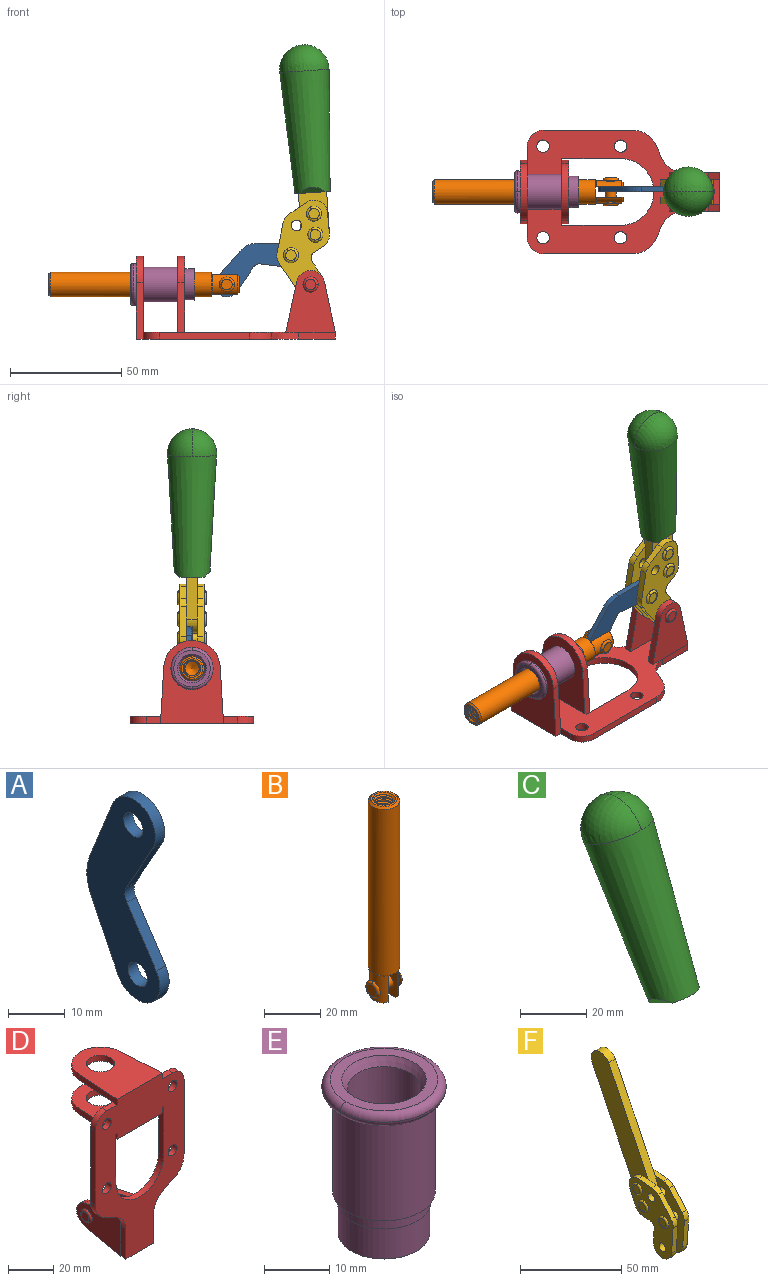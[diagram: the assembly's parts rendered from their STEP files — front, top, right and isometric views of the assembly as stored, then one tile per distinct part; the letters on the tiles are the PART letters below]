
ASSEMBLY  parts=6 mates=6
PART A: 12 faces, bbox 2.3x18.2x42.8 mm
  f0: cylinder r=2.4mm len=4.8mm, axis (1,0,0), area 34.9mm2, adj f4,f11
  f1: cylinder r=10.41mm len=8.47mm, axis (1,0,0), area 20.2mm2, adj f4,f9,f10,f11
  f2: cylinder r=3.05mm len=3.16mm, axis (1,0,0), area 7.7mm2, adj f4,f6,f7,f11
  f3: cylinder r=2.4mm len=4.8mm, axis (1,0,0), area 34.9mm2, adj f4,f11
  f4: plane 42.81x18.23mm, normal (-1,0,0), area 414.1mm2, adj f0,f1,f2,f3,f5,f6,f7,f8
  f5: cylinder r=5.54mm len=10.67mm, axis (1,0,0), area 41.8mm2, adj f4,f6,f10,f11
  f6: plane 11.66x6.53mm, normal (0,-0.87,-0.49), area 30.9mm2, adj f2,f4,f5,f11
  f7: plane 11.17x7.33mm, normal (0,-0.84,0.55), area 30.9mm2, adj f2,f4,f8,f11
  f8: cylinder r=5.54mm len=10.51mm, axis (1,0,0), area 41.8mm2, adj f4,f7,f9,f11
  f9: plane 13.67x6.67mm, normal (0,0.9,-0.44), area 35.1mm2, adj f1,f4,f8,f11
  f10: plane 14.1x5.7mm, normal (0,0.93,0.37), area 35.1mm2, adj f1,f4,f5,f11
  f11: plane 42.81x18.23mm, normal (1,0,0), area 414.1mm2, adj f0,f1,f2,f3,f5,f6,f7,f8
PART B: 48 faces, bbox 12.6x11.1x86.1 mm
  f0: torus R=2.41mm, axis (-1,0,0), area 15mm2, adj f30,f32,f34
  f1: torus R=2.41mm, axis (-1,0,0), area 15mm2, adj f29,f31,f33
  f2: cylinder r=5.54mm len=72.39mm, axis (0,0,1), area 2518.5mm2, adj f3,f4,f42,f43
  f3: cone r=5.54mm half-angle=45deg, axis (0,0,1), area 7.6mm2, adj f2,f5,f41
  f4: cone r=5.54mm half-angle=45deg, axis (0,0,-1), area 34.9mm2, adj f2,f39
  f5: cylinder r=5.08mm len=11.48mm, axis (0,0,1), area 108.3mm2, adj f3,f7,f8,f41
  f6: cylinder r=2.41mm len=4.83mm, axis (-1,0,0), area 71.2mm2, adj f40,f41
  f7: cylinder r=2.41mm len=4.83mm, axis (-1,0,0), area 7.6mm2, adj f5,f34
  f8: cone r=5.08mm half-angle=45deg, axis (0,0,1), area 10.6mm2, adj f5,f37,f41
  f9: cone r=3.98mm half-angle=45deg, axis (0,0,1), area 17.6mm2, adj f27,f39,f45,f46,f47
  f10: cylinder r=2.41mm len=4.83mm, axis (-1,0,0), area 7.6mm2, adj f33,f38
  f11: cylinder r=3.2mm len=6.4mm, axis (0,0,1), area 78.4mm2, adj f12,f28,f44,f45,f47
  f12: cylinder r=3.2mm len=6.4mm, axis (0,0,1), area 10.5mm2, adj f11,f13,f45,f47
  f13: cylinder r=3.2mm len=6.4mm, axis (0,0,1), area 10.5mm2, adj f12,f14,f45,f47
  f14: cylinder r=3.2mm len=6.4mm, axis (0,0,1), area 10.5mm2, adj f13,f15,f45,f47
  f15: cylinder r=3.2mm len=6.4mm, axis (0,0,1), area 10.5mm2, adj f14,f16,f45,f47
  f16: cylinder r=3.2mm len=6.4mm, axis (0,0,1), area 10.5mm2, adj f15,f17,f45,f47
  f17: cylinder r=3.2mm len=6.4mm, axis (0,0,1), area 10.5mm2, adj f16,f18,f45,f47
  f18: cylinder r=3.2mm len=6.4mm, axis (0,0,1), area 10.5mm2, adj f17,f19,f45,f47
  f19: cylinder r=3.2mm len=6.4mm, axis (0,0,1), area 10.5mm2, adj f18,f20,f45,f47
  f20: cylinder r=3.2mm len=6.4mm, axis (0,0,1), area 10.5mm2, adj f19,f21,f45,f47
  f21: cylinder r=3.2mm len=6.4mm, axis (0,0,1), area 10.5mm2, adj f20,f22,f45,f47
  f22: cylinder r=3.2mm len=6.4mm, axis (0,0,1), area 10.5mm2, adj f21,f23,f45,f47
  f23: cylinder r=3.2mm len=6.4mm, axis (0,0,1), area 10.5mm2, adj f22,f24,f45,f47
  f24: cylinder r=3.2mm len=6.4mm, axis (0,0,1), area 10.5mm2, adj f23,f25,f45,f47
  f25: cylinder r=3.2mm len=6.4mm, axis (0,0,1), area 10.5mm2, adj f24,f26,f45,f47
  f26: cylinder r=3.2mm len=6.4mm, axis (0,0,1), area 10.5mm2, adj f25,f27,f45,f47
  f27: cylinder r=3.2mm len=6.4mm, axis (0,0,1), area 7.4mm2, adj f9,f26,f45,f47
  f28: cone r=3.2mm half-angle=60deg, axis (0,0,1), area 37.2mm2, adj f11
  f29: plane 4.83x4.83mm, normal (-1,0,0), area 18.3mm2, adj f1,f31
  f30: plane 4.83x4.83mm, normal (1,0,0), area 18.3mm2, adj f0,f32
  f31: torus R=2.41mm, axis (-1,0,0), area 15mm2, adj f1,f29,f33
  f32: torus R=2.41mm, axis (-1,0,0), area 15mm2, adj f0,f30,f34
  f33: plane 6.83x6.83mm, normal (1,0,0), area 18.3mm2, adj f1,f10,f31
  f34: plane 6.83x6.83mm, normal (-1,0,0), area 18.3mm2, adj f0,f7,f32
  f35: cone r=5.08mm half-angle=45deg, axis (0,0,1), area 10.6mm2, adj f36,f38,f40
  f36: plane 7.25x1.97mm, normal (0,0,-1), area 10mm2, adj f35,f40
  f37: plane 7.25x1.97mm, normal (0,0,-1), area 10mm2, adj f8,f41
  f38: cylinder r=5.08mm len=11.48mm, axis (0,0,1), area 108.3mm2, adj f10,f35,f40,f42
  f39: plane 9.55x9.55mm, normal (0,0,1), area 22mm2, adj f4,f9
  f40: plane 12.76x10.09mm, normal (1,0,0), area 95.7mm2, adj f6,f35,f36,f38,f42,f43
  f41: plane 12.76x10.09mm, normal (-1,0,0), area 95.7mm2, adj f3,f5,f6,f8,f37,f43
  f42: cone r=5.54mm half-angle=45deg, axis (0,0,1), area 7.6mm2, adj f2,f38,f40
  f43: plane 11.07x4.7mm, normal (0,0,-1), area 50.4mm2, adj f2,f40,f41
  f44: plane 0.89x0.62mm, normal (-1,0,0), area 0.3mm2, adj f11,f45,f46,f47
  f45: bspline ~24.8x7.63mm, area 266.6mm2, adj f9,f11,f12,f13,f14,f15,f16,f17
  f46: bspline ~24.87x7.63mm, area 73.6mm2, adj f9,f44,f45,f47
  f47: bspline ~24.98x7.63mm, area 272.5mm2, adj f9,f11,f12,f13,f14,f15,f16,f17
PART C: 11 faces, bbox 22.3x42.6x64.5 mm
  f0: sphere r=11.13mm, area 411.4mm2, adj f1,f8
  f1: cone r=11.11mm half-angle=3.3deg, axis (0,0.44,0.9), area 3251.8mm2, adj f0,f7,f8,f9,f10
  f2: cylinder r=6.16mm len=11.7mm, axis (1,0,0), area 89.5mm2, adj f3,f4,f5,f6
  f3: plane 60.23x36.75mm, normal (-1,0,0), area 763.6mm2, adj f2,f4,f6,f10
  f4: plane 51.37x25.05mm, normal (0,0.9,-0.44), area 264.2mm2, adj f2,f3,f5,f10
  f5: plane 60.23x36.75mm, normal (1,0,0), area 763.6mm2, adj f2,f4,f6,f10
  f6: plane 51.37x25.05mm, normal (0,-0.9,0.44), area 264.2mm2, adj f2,f3,f5,f10
  f7: plane 9.95x5.95mm, normal (0.71,-0.31,-0.64), area 25.8mm2, adj f1,f10
  f8: sphere r=11.13mm, area 411.4mm2, adj f0,f1
  f9: plane 9.95x5.95mm, normal (-0.71,-0.31,-0.64), area 25.8mm2, adj f1,f10
  f10: plane 14.27x11.38mm, normal (0,-0.44,-0.9), area 106.7mm2, adj f1,f3,f4,f5,f6,f7,f9
PART D: 55 faces, bbox 55.7x37.4x89.8 mm
  f0: torus R=2.41mm, axis (-1,0,0), area 15mm2, adj f11,f15,f25
  f1: torus R=2.41mm, axis (-1,0,0), area 15mm2, adj f10,f12,f22
  f2: cylinder r=2.78mm len=5.56mm, axis (0,-1,0), area 54.2mm2, adj f30,f54
  f3: cylinder r=14.99mm len=29.97mm, axis (0,-1,0), area 145.9mm2, adj f30,f49,f53,f54
  f4: cylinder r=2.78mm len=5.56mm, axis (0,-1,0), area 54.2mm2, adj f30,f54
  f5: cylinder r=2.78mm len=5.56mm, axis (0,-1,0), area 54.2mm2, adj f30,f54
  f6: cylinder r=2.78mm len=5.56mm, axis (0,-1,0), area 54.2mm2, adj f30,f54
  f7: cylinder r=6.35mm len=12.7mm, axis (0,0,1), area 123.6mm2, adj f27,f51
  f8: cylinder r=6.35mm len=12.7mm, axis (0,0,-1), area 124.7mm2, adj f21,f35
  f9: cylinder r=2.41mm len=11.18mm, axis (-1,0,0), area 169.4mm2, adj f16,f19
  f10: plane 4.83x4.83mm, normal (1,0,0), area 18.3mm2, adj f1,f12
  f11: plane 4.83x4.83mm, normal (-1,0,0), area 18.3mm2, adj f0,f15
  f12: torus R=2.41mm, axis (-1,0,0), area 15mm2, adj f1,f10,f22
  f13: cylinder r=6.35mm len=12.41mm, axis (1,0,0), area 53.4mm2, adj f18,f19,f22,f23
  f14: cylinder r=6.35mm len=12.41mm, axis (-1,0,0), area 53.4mm2, adj f16,f17,f24,f25
  f15: torus R=2.41mm, axis (-1,0,0), area 15mm2, adj f0,f11,f25
  f16: plane 27.86x22.35mm, normal (1,0,0), area 425.4mm2, adj f9,f14,f17,f24,f30
  f17: plane 22.86x4.97mm, normal (0,0.21,0.98), area 72.5mm2, adj f14,f16,f25,f30
  f18: plane 22.86x4.97mm, normal (0,0.21,0.98), area 72.5mm2, adj f13,f19,f22,f30
  f19: plane 27.86x22.35mm, normal (-1,0,0), area 425.4mm2, adj f9,f13,f18,f23,f30
  f20: cylinder r=12.7mm len=25.35mm, axis (0,0,-1), area 119.8mm2, adj f21,f34,f35,f36
  f21: plane 34.21x28.07mm, normal (0,0,-1), area 702.4mm2, adj f8,f20,f30,f34,f36
  f22: plane 27.96x22.45mm, normal (1,0,0), area 407.2mm2, adj f1,f12,f13,f18,f23,f30,f42,f43
  f23: plane 22.86x4.97mm, normal (0,0.21,-0.98), area 72.5mm2, adj f13,f19,f22,f44
  f24: plane 22.86x4.97mm, normal (0,0.21,-0.98), area 72.5mm2, adj f14,f16,f25,f44
  f25: plane 27.86x22.35mm, normal (-1,0,0), area 407.1mm2, adj f0,f14,f15,f17,f24,f30,f45,f46
  f26: plane 3.1x0.95mm, normal (0,0,-1), area 2.7mm2, adj f30,f49,f50,f54
  f27: plane 34.21x28.07mm, normal (0,0,1), area 702.4mm2, adj f7,f28,f30,f50,f52
  f28: cylinder r=12.7mm len=25.35mm, axis (0,0,1), area 118.8mm2, adj f27,f50,f51,f52
  f29: plane 3.1x0.95mm, normal (0,0,-1), area 2.7mm2, adj f30,f52,f53,f54
  f30: plane 86.54x55.63mm, normal (0,1,0), area 2362.9mm2, adj f2,f3,f4,f5,f6,f16,f17,f18
  f31: plane 40.56x3.1mm, normal (-1,0,0), area 125.7mm2, adj f30,f32,f48,f54
  f32: cylinder r=7.11mm len=7.11mm, axis (0,-1,0), area 34.6mm2, adj f30,f31,f33,f54
  f33: plane 6.67x3.1mm, normal (0,0,1), area 20.4mm2, adj f30,f32,f34,f54
  f34: plane 25.39x3.13mm, normal (-1,0.06,0), area 79.5mm2, adj f20,f21,f33,f35,f54
  f35: plane 37.31x28.45mm, normal (0,0,1), area 789.9mm2, adj f8,f20,f34,f36,f54
  f36: plane 25.39x3.13mm, normal (1,0.06,0), area 79.5mm2, adj f20,f21,f35,f37,f54
  f37: plane 6.67x3.1mm, normal (0,0,1), area 20.4mm2, adj f30,f36,f38,f54
  f38: cylinder r=7.11mm len=7.11mm, axis (0,-1,0), area 34.6mm2, adj f30,f37,f39,f54
  f39: plane 40.56x3.1mm, normal (1,0,0), area 125.7mm2, adj f30,f38,f40,f54
  f40: cylinder r=11.18mm len=10.16mm, axis (0,-1,0), area 39.5mm2, adj f30,f39,f41,f54
  f41: plane 6.09x3.1mm, normal (0.42,0,-0.91), area 20.8mm2, adj f30,f40,f42,f54
  f42: cylinder r=11.18mm len=9.41mm, axis (0,-1,0), area 37.2mm2, adj f22,f30,f41,f43,f54
  f43: plane 16.5x3.1mm, normal (1,0,0), area 51.1mm2, adj f22,f42,f44,f54
  f44: plane 17.37x3.1mm, normal (0,0,-1), area 53.8mm2, adj f23,f24,f30,f43,f45,f54
  f45: plane 16.5x3.1mm, normal (-1,0,0), area 51.1mm2, adj f25,f44,f46,f54
  f46: cylinder r=11.18mm len=9.41mm, axis (0,-1,0), area 37.2mm2, adj f25,f30,f45,f47,f54
  f47: plane 6.09x3.1mm, normal (-0.42,0,-0.91), area 20.8mm2, adj f30,f46,f48,f54
  f48: cylinder r=11.18mm len=10.16mm, axis (0,-1,0), area 39.5mm2, adj f30,f31,f47,f54
  f49: plane 26.54x3.1mm, normal (-1,0,0), area 82.3mm2, adj f3,f26,f30,f54
  f50: plane 25.39x3.1mm, normal (1,0.06,0), area 78.8mm2, adj f26,f27,f28,f51,f54
  f51: plane 37.31x28.45mm, normal (0,0,-1), area 789.9mm2, adj f7,f28,f50,f52,f54
  f52: plane 25.39x3.1mm, normal (-1,0.06,0), area 78.8mm2, adj f27,f28,f29,f51,f54
  f53: plane 26.54x3.1mm, normal (1,0,0), area 82.3mm2, adj f3,f29,f30,f54
  f54: plane 89.66x55.63mm, normal (0,-1,0), area 2678.5mm2, adj f2,f3,f4,f5,f6,f26,f29,f31
PART E: 15 faces, bbox 20.6x20.6x28.7 mm
  f0: torus R=8.26mm, axis (0,0,1), area 56.8mm2, adj f1,f10,f12
  f1: torus R=8.26mm, axis (0,0,1), area 56.8mm2, adj f0,f6,f13
  f2: cylinder r=5.59mm len=25.91mm, axis (0,0,1), area 909.6mm2, adj f3,f4
  f3: cone r=6.86mm half-angle=45deg, axis (0,0,-1), area 70.2mm2, adj f2,f14
  f4: cone r=6.47mm half-angle=30deg, axis (0,0,1), area 66.7mm2, adj f2,f13
  f5: cylinder r=7.04mm len=14.07mm, axis (0,0,1), area 252.6mm2, adj f11,f14
  f6: torus R=8.26mm, axis (0,0,1), area 56.8mm2, adj f1,f12,f13
  f7: cylinder r=7.16mm len=14.33mm, axis (0,0,1), area 91.5mm2, adj f9,f11
  f8: cylinder r=7.86mm len=18.42mm, axis (0,0,1), area 909.6mm2, adj f9,f10
  f9: plane 15.72x15.72mm, normal (0,0,-1), area 33mm2, adj f7,f8
  f10: plane 16.51x16.51mm, normal (0,0,-1), area 19.9mm2, adj f0,f8,f12
  f11: plane 14.33x14.33mm, normal (0,0,-1), area 5.7mm2, adj f5,f7
  f12: torus R=8.26mm, axis (0,0,1), area 56.8mm2, adj f0,f6,f10
  f13: plane 16.51x16.51mm, normal (0,0,1), area 82.7mm2, adj f1,f4,f6
  f14: plane 14.07x14.07mm, normal (0,0,-1), area 7.8mm2, adj f3,f5
PART F: 59 faces, bbox 12.9x60.2x99.6 mm
  f0: torus R=2.39mm, axis (-1,0,0), area 14.9mm2, adj f20,f43,f51
  f1: torus R=2.39mm, axis (-1,0,0), area 14.9mm2, adj f19,f42,f51
  f2: torus R=2.39mm, axis (-1,0,0), area 14.9mm2, adj f18,f35,f51
  f3: torus R=2.39mm, axis (-1,0,0), area 14.9mm2, adj f14,f17,f23
  f4: torus R=2.39mm, axis (-1,0,0), area 14.9mm2, adj f13,f16,f23
  f5: torus R=2.39mm, axis (-1,0,0), area 14.9mm2, adj f12,f15,f23
  f6: cylinder r=2.39mm len=4.78mm, axis (1,0,0), area 46.5mm2, adj f48,f50,f51
  f7: cylinder r=2.39mm len=4.78mm, axis (1,0,0), area 46.5mm2, adj f50,f51
  f8: cylinder r=6.35mm len=12.68mm, axis (1,0,0), area 61.8mm2, adj f38,f39,f50,f51
  f9: cylinder r=2.39mm len=4.78mm, axis (-1,0,0), area 70.5mm2, adj f46,f50
  f10: cylinder r=2.39mm len=4.78mm, axis (-1,0,0), area 46.5mm2, adj f23,f45,f46
  f11: cylinder r=2.39mm len=4.78mm, axis (-1,0,0), area 46.5mm2, adj f23,f46
  f12: plane 4.78x4.78mm, normal (1,0,0), area 17.9mm2, adj f5,f15
  f13: plane 4.78x4.78mm, normal (1,0,0), area 17.9mm2, adj f4,f16
  f14: plane 4.78x4.78mm, normal (1,0,0), area 17.9mm2, adj f3,f17
  f15: torus R=2.39mm, axis (-1,0,0), area 14.9mm2, adj f5,f12,f23
  f16: torus R=2.39mm, axis (-1,0,0), area 14.9mm2, adj f4,f13,f23
  f17: torus R=2.39mm, axis (-1,0,0), area 14.9mm2, adj f3,f14,f23
  f18: plane 4.78x4.78mm, normal (-1,0,0), area 17.9mm2, adj f2,f35
  f19: plane 4.78x4.78mm, normal (-1,0,0), area 17.9mm2, adj f1,f42
  f20: plane 4.78x4.78mm, normal (-1,0,0), area 17.9mm2, adj f0,f43
  f21: plane 2.26x0.2mm, normal (1,0,0), area 0.2mm2, adj f31,f44
  f22: plane 2.26x0.2mm, normal (-1,0,0), area 0.2mm2, adj f41,f44
  f23: plane 39.37x30.77mm, normal (1,0,0), area 565.5mm2, adj f3,f4,f5,f10,f11,f15,f16,f17
  f24: cylinder r=6.1mm len=4.15mm, axis (-1,0,0), area 14.7mm2, adj f23,f25,f32,f46
  f25: plane 10.25x9.01mm, normal (0,-0.75,0.66), area 42.3mm2, adj f23,f24,f26,f46
  f26: cylinder r=6.35mm len=4.64mm, axis (-1,0,0), area 15.6mm2, adj f23,f25,f27,f46
  f27: plane 15.84x3.1mm, normal (0,-1,-0.07), area 49.2mm2, adj f23,f26,f28,f46
  f28: cylinder r=6.35mm len=12.68mm, axis (-1,0,0), area 61.8mm2, adj f23,f27,f29,f46
  f29: plane 8.11x3.1mm, normal (0,1,0.07), area 25.2mm2, adj f23,f28,f30,f46
  f30: cylinder r=3.05mm len=3.25mm, axis (-1,0,0), area 14.8mm2, adj f23,f29,f31,f46
  f31: plane 5.99x3.1mm, normal (0,0.07,-1), area 18.6mm2, adj f21,f23,f30,f44,f46
  f32: plane 9.5x3.1mm, normal (0,-0.07,1), area 29.5mm2, adj f23,f24,f33,f46,f47
  f33: cylinder r=6.1mm len=8.63mm, axis (-1,0,0), area 39.1mm2, adj f23,f32,f34,f47
  f34: plane 8.65x3.96mm, normal (0,0.91,-0.42), area 29.5mm2, adj f23,f33,f44,f47
  f35: torus R=2.39mm, axis (-1,0,0), area 14.9mm2, adj f2,f18,f51
  f36: plane 10.25x9.01mm, normal (0,-0.75,0.66), area 42.3mm2, adj f37,f49,f50,f51
  f37: cylinder r=6.35mm len=4.64mm, axis (1,0,0), area 15.6mm2, adj f36,f38,f50,f51
  f38: plane 15.84x3.1mm, normal (0,-1,-0.07), area 49.2mm2, adj f8,f37,f50,f51
  f39: plane 8.11x3.1mm, normal (0,1,0.07), area 25.2mm2, adj f8,f40,f50,f51
  f40: cylinder r=3.05mm len=3.25mm, axis (1,0,0), area 14.8mm2, adj f39,f41,f50,f51
  f41: plane 5.99x3.1mm, normal (0,0.07,-1), area 18.6mm2, adj f22,f40,f44,f50,f51
  f42: torus R=2.39mm, axis (-1,0,0), area 14.9mm2, adj f1,f19,f51
  f43: torus R=2.39mm, axis (-1,0,0), area 14.9mm2, adj f0,f20,f51
  f44: cylinder r=6.35mm len=12.12mm, axis (-1,0,0), area 128.9mm2, adj f21,f22,f23,f31,f34,f41,f46,f47
  f45: plane 2.65x1.35mm, normal (1,0,0), area 1mm2, adj f10,f55
  f46: plane 39.08x20.42mm, normal (-1,0,0), area 412.5mm2, adj f9,f10,f11,f24,f25,f26,f27,f28
  f47: plane 77.62x39.82mm, normal (1,0,0), area 850mm2, adj f32,f33,f34,f44,f53,f54,f55
  f48: plane 2.65x1.35mm, normal (-1,0,0), area 1mm2, adj f6,f55
  f49: cylinder r=6.1mm len=4.15mm, axis (1,0,0), area 14.7mm2, adj f36,f50,f51,f56
  f50: plane 39.08x20.42mm, normal (1,0,0), area 412.5mm2, adj f6,f7,f8,f9,f36,f37,f38,f39
  f51: plane 39.37x30.77mm, normal (-1,0,0), area 565.5mm2, adj f0,f1,f2,f6,f7,f8,f35,f36
  f52: plane 8.65x3.96mm, normal (0,0.91,-0.42), area 29.5mm2, adj f44,f51,f57,f58
  f53: plane 68.49x33.4mm, normal (0,0.9,-0.44), area 358.1mm2, adj f44,f47,f54,f58
  f54: cylinder r=6.35mm len=12.06mm, axis (1,0,0), area 93.7mm2, adj f47,f53,f55,f58
  f55: plane 68.49x33.4mm, normal (0,-0.9,0.44), area 358.1mm2, adj f44,f45,f46,f47,f48,f50,f54,f58
  f56: plane 9.5x3.1mm, normal (0,-0.07,1), area 29.5mm2, adj f49,f50,f51,f57,f58
  f57: cylinder r=6.1mm len=8.63mm, axis (1,0,0), area 39.1mm2, adj f51,f52,f56,f58
  f58: plane 77.62x39.82mm, normal (-1,0,0), area 850mm2, adj f44,f52,f53,f54,f55,f56,f57
PLACE A rot(axis=(0.65,-0.65,-0.4),136.3deg) t=(19.21,1.16,9.51)mm
PLACE B rot(axis=(0.58,-0.58,-0.58),120deg) t=(9.85,0,0)mm
PLACE C rot(axis=(0.25,-0.25,-0.94),93.8deg) t=(-5.22,-0.04,40.21)mm
PLACE D rot(axis=(0.58,-0.58,-0.58),120deg) t=(0,0,0)mm fixed
PLACE E rot(axis=(0,-1,0),90deg) t=(0,-24.61,24.61)mm
PLACE F rot(axis=(0.25,-0.25,-0.94),93.8deg) t=(-5.22,0,40.21)mm
MATE revolute A.f3 <-> F.f4  axis (0,-1,0) through (23.26,0,37.8)mm
MATE revolute F.f7 <-> D.f0  axis (0,1,0) through (32.09,0,24.61)mm
MATE fastened C.f2 <-> F.f54  axis (0,1,0) through (29.16,-2.35,123.06)mm
MATE fastened E.f2 <-> D.f7  axis (-1,0,0) through (-46.39,0,24.61)mm
MATE revolute A.f5 <-> B.f6  axis (0,-1,0) through (-5.63,0,24.61)mm
MATE fastened B.f2 <-> E.f12  axis (-1,0,0) through (-48.93,0,24.61)mm
